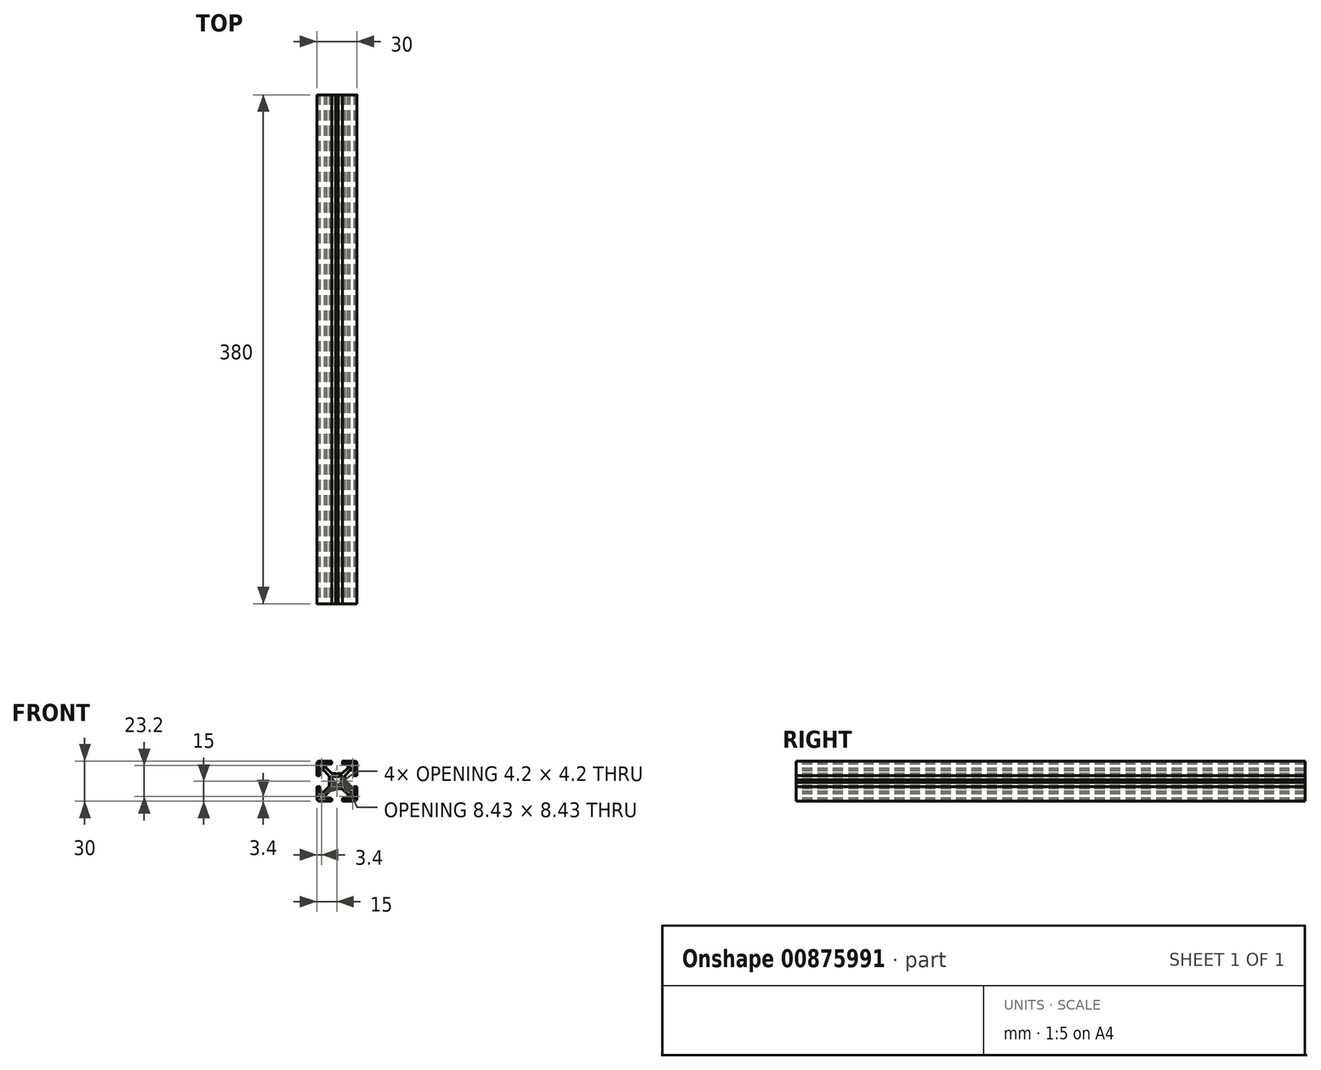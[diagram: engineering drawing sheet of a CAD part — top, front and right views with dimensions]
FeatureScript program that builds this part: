
annotation { "Feature Type Name" : "Feature", "Feature Type Description" : "" }
export const myFeature = defineFeature(function(context is Context, id is Id, definition is map)
    precondition{}
    {
        {
            var Q0;
            Q0=qCreatedBy(makeId("Front.planeOp"),FACE);
            var sketch = newSketch(context, id + "F0", { "sketchPlane" : qUnion([Q0])});
            skArc(sketch, "E0", {"start": v(9.88, 13.7) * mm, "mid": v(9.61, 13.59) * mm, "end": v(9.5, 13.32) * mm});
            skLineSegment(sketch, "E1", {"start": v(12.7, 13.7) * mm, "end": v(9.88, 13.7) * mm});
            skArc(sketch, "E2", {"start": v(13.7, 12.7) * mm, "mid": v(13.4, 13.4) * mm, "end": v(12.7, 13.7) * mm});
            skLineSegment(sketch, "E3", {"start": v(13.7, 9.88) * mm, "end": v(13.7, 12.7) * mm});
            skArc(sketch, "E4", {"start": v(13.32, 9.5) * mm, "mid": v(13.59, 9.61) * mm, "end": v(13.7, 9.88) * mm});
            skLineSegment(sketch, "E5", {"start": v(9.88, 9.5) * mm, "end": v(13.32, 9.5) * mm});
            skArc(sketch, "E6", {"start": v(9.5, 9.88) * mm, "mid": v(9.61, 9.61) * mm, "end": v(9.88, 9.5) * mm});
            skLineSegment(sketch, "E7", {"start": v(9.5, 13.32) * mm, "end": v(9.5, 9.88) * mm});
            skArc(sketch, "E8", {"start": v(-9.5, 13.32) * mm, "mid": v(-9.61, 13.59) * mm, "end": v(-9.88, 13.7) * mm});
            skLineSegment(sketch, "E9", {"start": v(-9.5, 9.88) * mm, "end": v(-9.5, 13.32) * mm});
            skArc(sketch, "E10", {"start": v(-9.88, 9.5) * mm, "mid": v(-9.61, 9.61) * mm, "end": v(-9.5, 9.88) * mm});
            skLineSegment(sketch, "E11", {"start": v(-13.32, 9.5) * mm, "end": v(-9.88, 9.5) * mm});
            skArc(sketch, "E12", {"start": v(-13.7, 9.88) * mm, "mid": v(-13.59, 9.61) * mm, "end": v(-13.32, 9.5) * mm});
            skLineSegment(sketch, "E13", {"start": v(-13.7, 12.7) * mm, "end": v(-13.7, 9.88) * mm});
            skArc(sketch, "E14", {"start": v(-12.7, 13.7) * mm, "mid": v(-13.4, 13.4) * mm, "end": v(-13.7, 12.7) * mm});
            skLineSegment(sketch, "E15", {"start": v(-9.88, 13.7) * mm, "end": v(-12.7, 13.7) * mm});
            skArc(sketch, "E16", {"start": v(-1.5, -3.2) * mm, "mid": v(0, -3.53) * mm, "end": v(1.5, -3.2) * mm});
            skLineSegment(sketch, "E17", {"start": v(-2.47, -3.98) * mm, "end": v(-1.5, -3.2) * mm});
            skArc(sketch, "E18", {"start": v(-3.98, -2.47) * mm, "mid": v(-3.9, -3.9) * mm, "end": v(-2.47, -3.98) * mm});
            skLineSegment(sketch, "E19", {"start": v(-3.2, -1.5) * mm, "end": v(-3.98, -2.47) * mm});
            skArc(sketch, "E20", {"start": v(-3.2, 1.5) * mm, "mid": v(-3.53, 0) * mm, "end": v(-3.2, -1.5) * mm});
            skLineSegment(sketch, "E21", {"start": v(-3.98, 2.47) * mm, "end": v(-3.2, 1.5) * mm});
            skArc(sketch, "E22", {"start": v(-2.47, 3.98) * mm, "mid": v(-3.9, 3.9) * mm, "end": v(-3.98, 2.47) * mm});
            skLineSegment(sketch, "E23", {"start": v(-1.5, 3.2) * mm, "end": v(-2.47, 3.98) * mm});
            skArc(sketch, "E24", {"start": v(1.5, 3.2) * mm, "mid": v(0, 3.53) * mm, "end": v(-1.5, 3.2) * mm});
            skLineSegment(sketch, "E25", {"start": v(2.47, 3.98) * mm, "end": v(1.5, 3.2) * mm});
            skArc(sketch, "E26", {"start": v(3.98, 2.47) * mm, "mid": v(3.9, 3.9) * mm, "end": v(2.47, 3.98) * mm});
            skLineSegment(sketch, "E27", {"start": v(3.2, 1.5) * mm, "end": v(3.98, 2.47) * mm});
            skArc(sketch, "E28", {"start": v(3.2, -1.5) * mm, "mid": v(3.53, 0) * mm, "end": v(3.2, 1.5) * mm});
            skLineSegment(sketch, "E29", {"start": v(3.98, -2.47) * mm, "end": v(3.2, -1.5) * mm});
            skArc(sketch, "E30", {"start": v(2.47, -3.98) * mm, "mid": v(3.9, -3.9) * mm, "end": v(3.98, -2.47) * mm});
            skLineSegment(sketch, "E31", {"start": v(1.5, -3.2) * mm, "end": v(2.47, -3.98) * mm});
            skArc(sketch, "E32", {"start": v(-13.32, -9.5) * mm, "mid": v(-13.59, -9.61) * mm, "end": v(-13.7, -9.88) * mm});
            skLineSegment(sketch, "E33", {"start": v(-9.88, -9.5) * mm, "end": v(-13.32, -9.5) * mm});
            skArc(sketch, "E34", {"start": v(-9.5, -9.88) * mm, "mid": v(-9.61, -9.61) * mm, "end": v(-9.88, -9.5) * mm});
            skLineSegment(sketch, "E35", {"start": v(-9.5, -13.32) * mm, "end": v(-9.5, -9.88) * mm});
            skArc(sketch, "E36", {"start": v(-9.88, -13.7) * mm, "mid": v(-9.61, -13.59) * mm, "end": v(-9.5, -13.32) * mm});
            skLineSegment(sketch, "E37", {"start": v(-12.7, -13.7) * mm, "end": v(-9.88, -13.7) * mm});
            skArc(sketch, "E38", {"start": v(-13.7, -12.7) * mm, "mid": v(-13.4, -13.4) * mm, "end": v(-12.7, -13.7) * mm});
            skLineSegment(sketch, "E39", {"start": v(-13.7, -9.88) * mm, "end": v(-13.7, -12.7) * mm});
            skArc(sketch, "E40", {"start": v(9.5, -13.32) * mm, "mid": v(9.61, -13.59) * mm, "end": v(9.88, -13.7) * mm});
            skLineSegment(sketch, "E41", {"start": v(9.5, -9.88) * mm, "end": v(9.5, -13.32) * mm});
            skArc(sketch, "E42", {"start": v(9.88, -9.5) * mm, "mid": v(9.61, -9.61) * mm, "end": v(9.5, -9.88) * mm});
            skLineSegment(sketch, "E43", {"start": v(13.32, -9.5) * mm, "end": v(9.88, -9.5) * mm});
            skArc(sketch, "E44", {"start": v(13.7, -9.88) * mm, "mid": v(13.59, -9.61) * mm, "end": v(13.32, -9.5) * mm});
            skLineSegment(sketch, "E45", {"start": v(13.7, -12.7) * mm, "end": v(13.7, -9.88) * mm});
            skArc(sketch, "E46", {"start": v(12.7, -13.7) * mm, "mid": v(13.4, -13.4) * mm, "end": v(13.7, -12.7) * mm});
            skLineSegment(sketch, "E47", {"start": v(9.88, -13.7) * mm, "end": v(12.7, -13.7) * mm});
            skArc(sketch, "E48", {"start": v(13.24, -4) * mm, "mid": v(12.89, -4.15) * mm, "end": v(12.74, -4.5) * mm});
            skLineSegment(sketch, "E49", {"start": v(12.74, -4.5) * mm, "end": v(12.74, -7.73) * mm});
            skArc(sketch, "E50", {"start": v(12.24, -8.25) * mm, "mid": v(12.6, -8.1) * mm, "end": v(12.74, -7.73) * mm});
            skLineSegment(sketch, "E51", {"start": v(12.24, -8.25) * mm, "end": v(10.26, -8.25) * mm});
            skArc(sketch, "E52", {"start": v(9.9, -8.1) * mm, "mid": v(10.07, -8.21) * mm, "end": v(10.26, -8.25) * mm});
            skLineSegment(sketch, "E53", {"start": v(9.9, -8.1) * mm, "end": v(5.98, -4.18) * mm});
            skArc(sketch, "E54", {"start": v(5.83, -3.82) * mm, "mid": v(5.87, -4.02) * mm, "end": v(5.98, -4.18) * mm});
            skLineSegment(sketch, "E55", {"start": v(5.83, -3.82) * mm, "end": v(5.83, -1.01) * mm});
            skLineSegment(sketch, "E56", {"start": v(5.83, -1.01) * mm, "end": v(5.32, -0.06) * mm});
            skLineSegment(sketch, "E57", {"start": v(5.32, -0.06) * mm, "end": v(5.83, 0.89) * mm});
            skLineSegment(sketch, "E58", {"start": v(5.83, 0.89) * mm, "end": v(5.83, 3.82) * mm});
            skArc(sketch, "E59", {"start": v(5.98, 4.18) * mm, "mid": v(5.87, 4.02) * mm, "end": v(5.83, 3.82) * mm});
            skLineSegment(sketch, "E60", {"start": v(5.98, 4.18) * mm, "end": v(9.9, 8.1) * mm});
            skArc(sketch, "E61", {"start": v(10.26, 8.25) * mm, "mid": v(10.07, 8.21) * mm, "end": v(9.9, 8.1) * mm});
            skLineSegment(sketch, "E62", {"start": v(10.26, 8.25) * mm, "end": v(12.24, 8.25) * mm});
            skArc(sketch, "E63", {"start": v(12.74, 7.73) * mm, "mid": v(12.6, 8.1) * mm, "end": v(12.24, 8.25) * mm});
            skLineSegment(sketch, "E64", {"start": v(12.74, 7.73) * mm, "end": v(12.74, 4.5) * mm});
            skArc(sketch, "E65", {"start": v(12.74, 4.5) * mm, "mid": v(12.89, 4.15) * mm, "end": v(13.24, 4) * mm});
            skLineSegment(sketch, "E66", {"start": v(13.24, 4) * mm, "end": v(14.5, 4) * mm});
            skArc(sketch, "E67", {"start": v(14.5, 4) * mm, "mid": v(14.85, 4.15) * mm, "end": v(15, 4.5) * mm});
            skLineSegment(sketch, "E68", {"start": v(15, 4.5) * mm, "end": v(15, 13) * mm});
            skArc(sketch, "E69", {"start": v(15, 13) * mm, "mid": v(14.41, 14.41) * mm, "end": v(13, 15) * mm});
            skLineSegment(sketch, "E70", {"start": v(13, 15) * mm, "end": v(4.5, 15) * mm});
            skArc(sketch, "E71", {"start": v(4.5, 15) * mm, "mid": v(4.15, 14.85) * mm, "end": v(4, 14.5) * mm});
            skLineSegment(sketch, "E72", {"start": v(4, 14.5) * mm, "end": v(4, 13.24) * mm});
            skArc(sketch, "E73", {"start": v(4, 13.24) * mm, "mid": v(4.15, 12.89) * mm, "end": v(4.5, 12.74) * mm});
            skLineSegment(sketch, "E74", {"start": v(4.5, 12.74) * mm, "end": v(7.73, 12.74) * mm});
            skArc(sketch, "E75", {"start": v(8.25, 12.24) * mm, "mid": v(8.1, 12.6) * mm, "end": v(7.73, 12.74) * mm});
            skLineSegment(sketch, "E76", {"start": v(8.25, 12.24) * mm, "end": v(8.25, 10.26) * mm});
            skArc(sketch, "E77", {"start": v(8.1, 9.9) * mm, "mid": v(8.21, 10.07) * mm, "end": v(8.25, 10.26) * mm});
            skLineSegment(sketch, "E78", {"start": v(8.1, 9.9) * mm, "end": v(4.18, 5.98) * mm});
            skArc(sketch, "E79", {"start": v(3.82, 5.83) * mm, "mid": v(4.02, 5.87) * mm, "end": v(4.18, 5.98) * mm});
            skLineSegment(sketch, "E80", {"start": v(3.82, 5.83) * mm, "end": v(0.95, 5.83) * mm});
            skLineSegment(sketch, "E81", {"start": v(0.95, 5.83) * mm, "end": v(0, 5.32) * mm});
            skLineSegment(sketch, "E82", {"start": v(0, 5.32) * mm, "end": v(-0.95, 5.83) * mm});
            skLineSegment(sketch, "E83", {"start": v(-0.95, 5.83) * mm, "end": v(-3.82, 5.83) * mm});
            skArc(sketch, "E84", {"start": v(-4.18, 5.98) * mm, "mid": v(-4.02, 5.87) * mm, "end": v(-3.82, 5.83) * mm});
            skLineSegment(sketch, "E85", {"start": v(-4.18, 5.98) * mm, "end": v(-8.1, 9.9) * mm});
            skArc(sketch, "E86", {"start": v(-8.25, 10.26) * mm, "mid": v(-8.21, 10.07) * mm, "end": v(-8.1, 9.9) * mm});
            skLineSegment(sketch, "E87", {"start": v(-8.25, 10.26) * mm, "end": v(-8.25, 12.24) * mm});
            skArc(sketch, "E88", {"start": v(-7.73, 12.74) * mm, "mid": v(-8.1, 12.6) * mm, "end": v(-8.25, 12.24) * mm});
            skLineSegment(sketch, "E89", {"start": v(-7.73, 12.74) * mm, "end": v(-4.5, 12.74) * mm});
            skArc(sketch, "E90", {"start": v(-4.5, 12.74) * mm, "mid": v(-4.15, 12.89) * mm, "end": v(-4, 13.24) * mm});
            skLineSegment(sketch, "E91", {"start": v(-4, 13.24) * mm, "end": v(-4, 14.5) * mm});
            skArc(sketch, "E92", {"start": v(-4, 14.5) * mm, "mid": v(-4.15, 14.85) * mm, "end": v(-4.5, 15) * mm});
            skLineSegment(sketch, "E93", {"start": v(-4.5, 15) * mm, "end": v(-13, 15) * mm});
            skArc(sketch, "E94", {"start": v(-13, 15) * mm, "mid": v(-14.41, 14.41) * mm, "end": v(-15, 13) * mm});
            skLineSegment(sketch, "E95", {"start": v(-15, 13) * mm, "end": v(-15, 4.5) * mm});
            skArc(sketch, "E96", {"start": v(-15, 4.5) * mm, "mid": v(-14.85, 4.15) * mm, "end": v(-14.5, 4) * mm});
            skLineSegment(sketch, "E97", {"start": v(-14.5, 4) * mm, "end": v(-13.24, 4) * mm});
            skArc(sketch, "E98", {"start": v(-13.24, 4) * mm, "mid": v(-12.89, 4.15) * mm, "end": v(-12.74, 4.5) * mm});
            skLineSegment(sketch, "E99", {"start": v(-12.74, 4.5) * mm, "end": v(-12.74, 7.73) * mm});
            skArc(sketch, "E100", {"start": v(-12.24, 8.25) * mm, "mid": v(-12.6, 8.1) * mm, "end": v(-12.74, 7.73) * mm});
            skLineSegment(sketch, "E101", {"start": v(-12.24, 8.25) * mm, "end": v(-10.26, 8.25) * mm});
            skArc(sketch, "E102", {"start": v(-9.9, 8.1) * mm, "mid": v(-10.07, 8.21) * mm, "end": v(-10.26, 8.25) * mm});
            skLineSegment(sketch, "E103", {"start": v(-9.9, 8.1) * mm, "end": v(-5.98, 4.18) * mm});
            skArc(sketch, "E104", {"start": v(-5.83, 3.82) * mm, "mid": v(-5.87, 4.02) * mm, "end": v(-5.98, 4.18) * mm});
            skLineSegment(sketch, "E105", {"start": v(-5.83, 3.82) * mm, "end": v(-5.83, 0.89) * mm});
            skLineSegment(sketch, "E106", {"start": v(-5.83, 0.89) * mm, "end": v(-5.32, -0.06) * mm});
            skLineSegment(sketch, "E107", {"start": v(-5.32, -0.06) * mm, "end": v(-5.83, -1.01) * mm});
            skLineSegment(sketch, "E108", {"start": v(-5.83, -1.01) * mm, "end": v(-5.83, -3.82) * mm});
            skArc(sketch, "E109", {"start": v(-5.98, -4.18) * mm, "mid": v(-5.87, -4.02) * mm, "end": v(-5.83, -3.82) * mm});
            skLineSegment(sketch, "E110", {"start": v(-5.98, -4.18) * mm, "end": v(-9.9, -8.1) * mm});
            skArc(sketch, "E111", {"start": v(-10.26, -8.25) * mm, "mid": v(-10.07, -8.21) * mm, "end": v(-9.9, -8.1) * mm});
            skLineSegment(sketch, "E112", {"start": v(-10.26, -8.25) * mm, "end": v(-12.24, -8.25) * mm});
            skArc(sketch, "E113", {"start": v(-12.74, -7.73) * mm, "mid": v(-12.6, -8.1) * mm, "end": v(-12.24, -8.25) * mm});
            skLineSegment(sketch, "E114", {"start": v(-12.74, -7.73) * mm, "end": v(-12.74, -4.5) * mm});
            skArc(sketch, "E115", {"start": v(-12.74, -4.5) * mm, "mid": v(-12.89, -4.15) * mm, "end": v(-13.24, -4) * mm});
            skLineSegment(sketch, "E116", {"start": v(-13.24, -4) * mm, "end": v(-14.5, -4) * mm});
            skArc(sketch, "E117", {"start": v(-14.5, -4) * mm, "mid": v(-14.85, -4.15) * mm, "end": v(-15, -4.5) * mm});
            skLineSegment(sketch, "E118", {"start": v(-15, -4.5) * mm, "end": v(-15, -13) * mm});
            skArc(sketch, "E119", {"start": v(-15, -13) * mm, "mid": v(-14.41, -14.41) * mm, "end": v(-13, -15) * mm});
            skLineSegment(sketch, "E120", {"start": v(-13, -15) * mm, "end": v(-4.5, -15) * mm});
            skArc(sketch, "E121", {"start": v(-4.5, -15) * mm, "mid": v(-4.15, -14.85) * mm, "end": v(-4, -14.5) * mm});
            skLineSegment(sketch, "E122", {"start": v(-4, -14.5) * mm, "end": v(-4, -13.24) * mm});
            skArc(sketch, "E123", {"start": v(-4, -13.24) * mm, "mid": v(-4.15, -12.89) * mm, "end": v(-4.5, -12.74) * mm});
            skLineSegment(sketch, "E124", {"start": v(-4.5, -12.74) * mm, "end": v(-7.73, -12.74) * mm});
            skArc(sketch, "E125", {"start": v(-8.25, -12.24) * mm, "mid": v(-8.1, -12.6) * mm, "end": v(-7.73, -12.74) * mm});
            skLineSegment(sketch, "E126", {"start": v(-8.25, -12.24) * mm, "end": v(-8.25, -10.26) * mm});
            skArc(sketch, "E127", {"start": v(-8.1, -9.9) * mm, "mid": v(-8.21, -10.07) * mm, "end": v(-8.25, -10.26) * mm});
            skLineSegment(sketch, "E128", {"start": v(-8.1, -9.9) * mm, "end": v(-4.18, -5.98) * mm});
            skArc(sketch, "E129", {"start": v(-3.82, -5.83) * mm, "mid": v(-4.02, -5.87) * mm, "end": v(-4.18, -5.98) * mm});
            skLineSegment(sketch, "E130", {"start": v(-3.82, -5.83) * mm, "end": v(-0.95, -5.83) * mm});
            skLineSegment(sketch, "E131", {"start": v(-0.95, -5.83) * mm, "end": v(0, -5.32) * mm});
            skLineSegment(sketch, "E132", {"start": v(0, -5.32) * mm, "end": v(0.95, -5.83) * mm});
            skLineSegment(sketch, "E133", {"start": v(0.95, -5.83) * mm, "end": v(3.82, -5.83) * mm});
            skArc(sketch, "E134", {"start": v(4.18, -5.98) * mm, "mid": v(4.02, -5.87) * mm, "end": v(3.82, -5.83) * mm});
            skLineSegment(sketch, "E135", {"start": v(4.18, -5.98) * mm, "end": v(8.1, -9.9) * mm});
            skArc(sketch, "E136", {"start": v(8.25, -10.26) * mm, "mid": v(8.21, -10.07) * mm, "end": v(8.1, -9.9) * mm});
            skLineSegment(sketch, "E137", {"start": v(8.25, -10.26) * mm, "end": v(8.25, -12.24) * mm});
            skArc(sketch, "E138", {"start": v(7.73, -12.74) * mm, "mid": v(8.1, -12.6) * mm, "end": v(8.25, -12.24) * mm});
            skLineSegment(sketch, "E139", {"start": v(7.73, -12.74) * mm, "end": v(4.5, -12.74) * mm});
            skArc(sketch, "E140", {"start": v(4.5, -12.74) * mm, "mid": v(4.15, -12.89) * mm, "end": v(4, -13.24) * mm});
            skLineSegment(sketch, "E141", {"start": v(4, -13.24) * mm, "end": v(4, -14.5) * mm});
            skArc(sketch, "E142", {"start": v(4, -14.5) * mm, "mid": v(4.15, -14.85) * mm, "end": v(4.5, -15) * mm});
            skLineSegment(sketch, "E143", {"start": v(4.5, -15) * mm, "end": v(13, -15) * mm});
            skArc(sketch, "E144", {"start": v(13, -15) * mm, "mid": v(14.41, -14.41) * mm, "end": v(15, -13) * mm});
            skLineSegment(sketch, "E145", {"start": v(15, -13) * mm, "end": v(15, -4.5) * mm});
            skArc(sketch, "E146", {"start": v(15, -4.5) * mm, "mid": v(14.85, -4.15) * mm, "end": v(14.5, -4) * mm});
            skLineSegment(sketch, "E147", {"start": v(14.5, -4) * mm, "end": v(13.24, -4) * mm});
            skSolve(sketch);
        }
        {
            var Q0;
            Q0=qCreatedBy(makeId("Top.planeOp"),FACE);
            var sketch = newSketch(context, id + "F1", { "sketchPlane" : qUnion([Q0])});
            skLineSegment(sketch, "E148", {"start": v(-1.5, 190) * mm, "end": v(-1.5, -190) * mm});
            skSolve(sketch);
        }
        {
            var Q0;
            Q0 = qSketchRegion(id + "F0", true);
            var Q1;
            Q1=sQuery(id+"F1.wireOp",EDGE,"E148");
            var Q2;
            Q2=sQuery(id+"F1.wireOp",EDGE,"fSjTIPXa-SZZ6-Uh3d-dTjF-iSAX6K3vTkU0");
            var Q3;
            Q3=sQuery(id+"F1.wireOp",EDGE,"X1iaMUp9-18Uv-Qplb-D4Eo-NhRo6oMLb04g");
            var Q4;
            Q4=sQuery(id+"F1.wireOp",EDGE,"ysMRVMGi-oqtn-a0SZ-pmm6-otZbrj3hBrry");
            sweep(context, id + "F2", {"profiles" : qUnion([Q0]), "path" : qUnion([Q1, Q2, Q3, Q4])});
        }
    });
